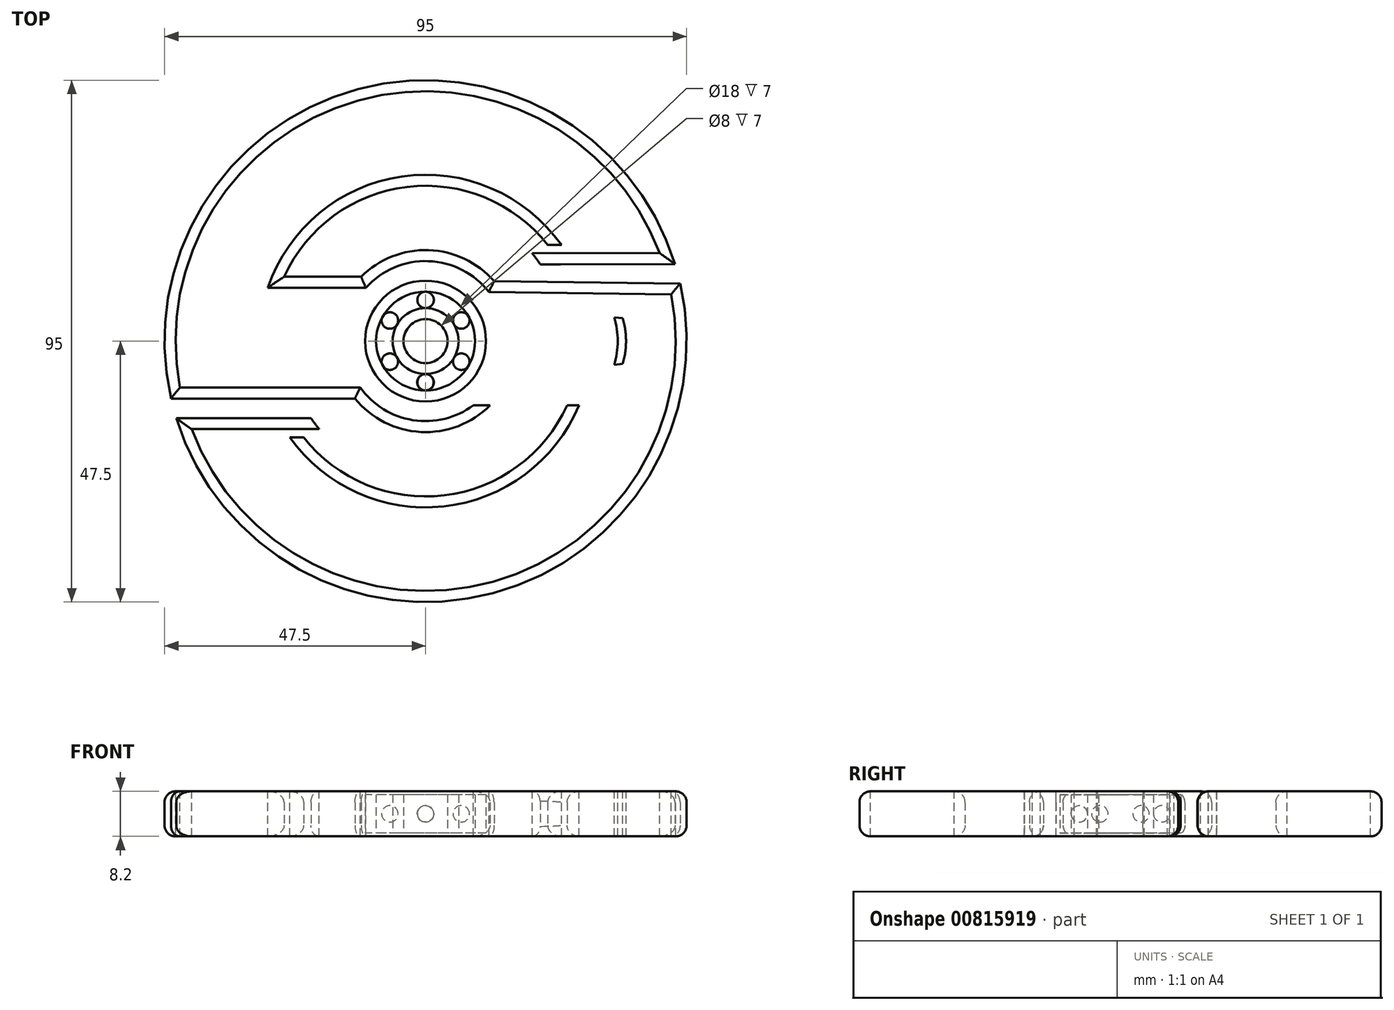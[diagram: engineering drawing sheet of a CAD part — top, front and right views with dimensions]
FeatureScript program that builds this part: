
annotation { "Feature Type Name" : "Feature", "Feature Type Description" : "" }
export const myFeature = defineFeature(function(context is Context, id is Id, definition is map)
    precondition{}
    {
        {
            var Q0;
            Q0=qCreatedBy(makeId("Top.planeOp"),FACE);
            var sketch = newSketch(context, id + "F0", { "sketchPlane" : qUnion([Q0])});
            skArc(sketch, "E0", {"start": v(45.38, 14.04) * mm, "mid": v(-10.46, 46.33) * mm, "end": v(-47, -6.81) * mm});
            skLineSegment(sketch, "E1.top", {"start": v(-45.38, -14.04) * mm, "end": v(-24.56, -14.04) * mm});
            skCircle(sketch, "E2", {"center": v(0, 0) * mm, "radius": 11.07 * mm});
            skArc(sketch, "E3", {"start": v(22.24, 17.5) * mm, "mid": v(-3.38, 28.09) * mm, "end": v(-25.75, 11.72) * mm});
            skArc(sketch, "E4.trimOffspring", {"start": v(-22.2, -17.54) * mm, "mid": v(3.4, -28.08) * mm, "end": v(25.75, -11.72) * mm});
            skArc(sketch, "E5.trimOffspring", {"start": v(-45.38, -14.04) * mm, "mid": v(10.5, -46.32) * mm, "end": v(47, 6.9) * mm});
            skLineSegment(sketch, "E6.trimOffspring", {"start": v(24.59, 14) * mm, "end": v(45.38, 14.04) * mm});
            skPoint(sketch, "E7.trimOffspring.end.orphan", {"position": v(45.38, -14.04) * mm});
            skPoint(sketch, "E1.bottom.start.orphan", {"position": v(-45.38, 14.04) * mm});
            skPoint(sketch, "E8.orphan", {"position": v(47, -6.9) * mm});
            skPoint(sketch, "E9.orphan", {"position": v(-47, 6.81) * mm});
            skArc(sketch, "E10", {"start": v(-12.86, -10.46) * mm, "mid": v(-0.85, -16.55) * mm, "end": v(11.72, -11.72) * mm});
            skArc(sketch, "E11.trimOffspring", {"start": v(12.47, 10.92) * mm, "mid": v(0.55, 16.57) * mm, "end": v(-11.72, 11.72) * mm});
            skLineSegment(sketch, "E12.trimOffspring", {"start": v(-8.7, 6.85) * mm, "end": v(8.59, 7) * mm});
            skLineSegment(sketch, "E13.trimOffspring", {"start": v(-8.7, -6.85) * mm, "end": v(8.69, -6.87) * mm});
            skLineSegment(sketch, "E14", {"start": v(-7.83, 7.83) * mm, "end": v(-6.87, 6.87) * mm});
            skLineSegment(sketch, "E15", {"start": v(6.87, -6.87) * mm, "end": v(7.83, -7.83) * mm});
            skLineSegment(sketch, "E16", {"start": v(-11.72, 11.72) * mm, "end": v(-25.75, 11.72) * mm});
            skLineSegment(sketch, "E17", {"start": v(11.72, -11.72) * mm, "end": v(11.72, -11.72) * mm});
            skArc(sketch, "E18", {"start": v(20.88, 14) * mm, "mid": v(19.54, 15.8) * mm, "end": v(18.05, 17.5) * mm});
            skLineSegment(sketch, "E19", {"start": v(-24.56, -14.04) * mm, "end": v(-20.85, -14.04) * mm});
            skLineSegment(sketch, "E20", {"start": v(24.59, 14) * mm, "end": v(20.88, 14) * mm});
            skLineSegment(sketch, "E21", {"start": v(22.24, 17.5) * mm, "end": v(18.05, 17.5) * mm});
            skLineSegment(sketch, "E22", {"start": v(-22.2, -17.54) * mm, "end": v(-18, -17.54) * mm});
            skArc(sketch, "E23.trimOffspring", {"start": v(-20.85, -14.04) * mm, "mid": v(-19.5, -15.85) * mm, "end": v(-18, -17.54) * mm});
            skLineSegment(sketch, "E24", {"start": v(0, 0) * mm, "end": v(0, 16.57) * mm, "construction": true});
            skLineSegment(sketch, "E25", {"start": v(-6.87, 6.87) * mm, "end": v(-11.72, 11.72) * mm, "construction": true});
            skLineSegment(sketch, "E26", {"start": v(0, 0) * mm, "end": v(11.72, 11.72) * mm, "construction": true});
            skLineSegment(sketch, "E27", {"start": v(6.87, -6.87) * mm, "end": v(11.72, -11.72) * mm, "construction": true});
            skLineSegment(sketch, "E28", {"start": v(0, 0) * mm, "end": v(0, -16.57) * mm, "construction": true});
            skLineSegment(sketch, "E29", {"start": v(0, 0) * mm, "end": v(-11.72, -11.72) * mm, "construction": true});
            skLineSegment(sketch, "E30.trimOffspring", {"start": v(-20, 20) * mm, "end": v(-33.59, 33.59) * mm, "construction": true});
            skLineSegment(sketch, "E31.trimOffspring", {"start": v(0, 28.29) * mm, "end": v(0, 47.5) * mm, "construction": true});
            skLineSegment(sketch, "E32.trimOffspring", {"start": v(20, 20) * mm, "end": v(33.59, 33.59) * mm, "construction": true});
            skLineSegment(sketch, "E33.trimOffspring", {"start": v(20, -20) * mm, "end": v(33.59, -33.59) * mm, "construction": true});
            skLineSegment(sketch, "E34.trimOffspring", {"start": v(0, -28.29) * mm, "end": v(0, -47.5) * mm, "construction": true});
            skLineSegment(sketch, "E35.trimOffspring", {"start": v(-20, -20) * mm, "end": v(-33.59, -33.59) * mm, "construction": true});
            skPoint(sketch, "E36", {"position": v(0, 37.9) * mm});
            skPoint(sketch, "E37", {"position": v(-26.8, 26.8) * mm});
            skPoint(sketch, "E38", {"position": v(26.8, 26.8) * mm});
            skPoint(sketch, "E39", {"position": v(26.8, -26.8) * mm});
            skPoint(sketch, "E40", {"position": v(0, -37.9) * mm});
            skPoint(sketch, "E41", {"position": v(-26.8, -26.8) * mm});
            skArc(sketch, "E42", {"start": v(-45.38, -14.04) * mm, "mid": v(10.5, -46.32) * mm, "end": v(47, 6.9) * mm, "construction": true});
            skArc(sketch, "E43", {"start": v(-47, -6.81) * mm, "mid": v(-46.7, -8.64) * mm, "end": v(-46.33, -10.46) * mm});
            skPoint(sketch, "E44", {"position": v(-46.33, -10.46) * mm});
            skArc(sketch, "E45", {"start": v(45.38, 14.04) * mm, "mid": v(-10.46, 46.33) * mm, "end": v(-47, -6.81) * mm, "construction": true});
            skArc(sketch, "E46", {"start": v(47, 6.9) * mm, "mid": v(46.7, 8.71) * mm, "end": v(46.32, 10.5) * mm});
            skPoint(sketch, "E47", {"position": v(46.32, 10.5) * mm});
            skLineSegment(sketch, "E48", {"start": v(-46.33, -10.46) * mm, "end": v(-36.42, -10.46) * mm});
            skLineSegment(sketch, "E49", {"start": v(46.32, 10.5) * mm, "end": v(12.47, 10.92) * mm});
            skPoint(sketch, "E50", {"position": v(-114.88, 3.23) * mm});
            skLineSegment(sketch, "E51.0", {"start": v(-114.88, 9.7) * mm, "end": v(-109.28, 6.47) * mm});
            skLineSegment(sketch, "E51.1", {"start": v(-109.28, 6.47) * mm, "end": v(-109.28, 0) * mm});
            skLineSegment(sketch, "E51.2", {"start": v(-109.28, 0) * mm, "end": v(-114.88, -3.23) * mm});
            skLineSegment(sketch, "E51.3", {"start": v(-114.88, -3.23) * mm, "end": v(-120.48, 0) * mm});
            skLineSegment(sketch, "E51.4", {"start": v(-120.48, 0) * mm, "end": v(-120.48, 6.47) * mm});
            skLineSegment(sketch, "E51.5", {"start": v(-120.48, 6.47) * mm, "end": v(-114.88, 9.7) * mm});
            skPoint(sketch, "E52", {"position": v(-130.27, -23) * mm});
            skLineSegment(sketch, "E53.0", {"start": v(-130.27, -16.53) * mm, "end": v(-124.67, -19.77) * mm});
            skLineSegment(sketch, "E53.1", {"start": v(-124.67, -19.77) * mm, "end": v(-124.67, -26.23) * mm});
            skLineSegment(sketch, "E53.2", {"start": v(-124.67, -26.23) * mm, "end": v(-130.27, -29.47) * mm});
            skLineSegment(sketch, "E53.3", {"start": v(-130.27, -29.47) * mm, "end": v(-135.87, -26.23) * mm});
            skLineSegment(sketch, "E53.4", {"start": v(-135.87, -26.23) * mm, "end": v(-135.87, -19.77) * mm});
            skLineSegment(sketch, "E53.5", {"start": v(-135.87, -19.77) * mm, "end": v(-130.27, -16.53) * mm});
            skLineSegment(sketch, "E54", {"start": v(-11.07, 0) * mm, "end": v(-47.5, 0) * mm, "construction": true});
            skLineSegment(sketch, "E55", {"start": v(11.07, 0) * mm, "end": v(47.5, 0) * mm, "construction": true});
            skLineSegment(sketch, "E56.0", {"start": v(-137.37, -18.9) * mm, "end": v(-130.27, -14.8) * mm});
            skLineSegment(sketch, "E56.1", {"start": v(-123.17, -18.9) * mm, "end": v(-123.17, -27.1) * mm});
            skLineSegment(sketch, "E56.2", {"start": v(-123.17, -27.1) * mm, "end": v(-130.27, -31.2) * mm});
            skLineSegment(sketch, "E56.3", {"start": v(-130.27, -14.8) * mm, "end": v(-123.17, -18.9) * mm});
            skLineSegment(sketch, "E56.4", {"start": v(-130.27, -31.2) * mm, "end": v(-137.37, -27.1) * mm});
            skLineSegment(sketch, "E56.5", {"start": v(-137.37, -27.1) * mm, "end": v(-137.37, -18.9) * mm});
            skLineSegment(sketch, "E57.0", {"start": v(-138.87, -18.03) * mm, "end": v(-130.27, -13.07) * mm});
            skLineSegment(sketch, "E57.1", {"start": v(-121.67, -18.03) * mm, "end": v(-121.67, -27.97) * mm});
            skLineSegment(sketch, "E57.2", {"start": v(-121.67, -27.97) * mm, "end": v(-130.27, -32.93) * mm});
            skLineSegment(sketch, "E57.3", {"start": v(-130.27, -13.07) * mm, "end": v(-121.67, -18.03) * mm});
            skLineSegment(sketch, "E57.4", {"start": v(-130.27, -32.93) * mm, "end": v(-138.87, -27.97) * mm});
            skLineSegment(sketch, "E57.5", {"start": v(-138.87, -27.97) * mm, "end": v(-138.87, -18.03) * mm});
            skPoint(sketch, "E58", {"position": v(-99.9, -24.26) * mm});
            skLineSegment(sketch, "E59.0", {"start": v(-109.83, -24.26) * mm, "end": v(-104.87, -15.66) * mm});
            skLineSegment(sketch, "E59.1", {"start": v(-94.94, -15.66) * mm, "end": v(-89.97, -24.26) * mm});
            skLineSegment(sketch, "E59.2", {"start": v(-89.97, -24.26) * mm, "end": v(-94.94, -32.86) * mm});
            skLineSegment(sketch, "E59.3", {"start": v(-104.87, -15.66) * mm, "end": v(-94.94, -15.66) * mm});
            skLineSegment(sketch, "E59.4", {"start": v(-94.94, -32.86) * mm, "end": v(-104.87, -32.86) * mm});
            skLineSegment(sketch, "E59.5", {"start": v(-104.87, -32.86) * mm, "end": v(-109.83, -24.26) * mm});
            skLineSegment(sketch, "E60.0", {"start": v(-107.82, -22.14) * mm, "end": v(-102.03, -16.34) * mm});
            skLineSegment(sketch, "E60.1", {"start": v(-94.1, -18.47) * mm, "end": v(-91.98, -26.38) * mm});
            skLineSegment(sketch, "E60.2", {"start": v(-91.98, -26.38) * mm, "end": v(-97.78, -32.18) * mm});
            skLineSegment(sketch, "E60.3", {"start": v(-102.03, -16.34) * mm, "end": v(-94.1, -18.47) * mm});
            skLineSegment(sketch, "E60.4", {"start": v(-97.78, -32.18) * mm, "end": v(-105.7, -30.06) * mm});
            skLineSegment(sketch, "E60.5", {"start": v(-105.7, -30.06) * mm, "end": v(-107.82, -22.14) * mm});
            skLineSegment(sketch, "E61.0", {"start": v(-99.9, -17.8) * mm, "end": v(-94.3, -21.03) * mm});
            skLineSegment(sketch, "E61.1", {"start": v(-94.3, -21.03) * mm, "end": v(-94.3, -27.5) * mm});
            skLineSegment(sketch, "E61.2", {"start": v(-94.3, -27.5) * mm, "end": v(-99.9, -30.73) * mm});
            skLineSegment(sketch, "E61.3", {"start": v(-99.9, -30.73) * mm, "end": v(-105.5, -27.5) * mm});
            skLineSegment(sketch, "E61.4", {"start": v(-105.5, -27.5) * mm, "end": v(-105.5, -21.03) * mm});
            skLineSegment(sketch, "E61.5", {"start": v(-105.5, -21.03) * mm, "end": v(-99.9, -17.8) * mm});
            skLineSegment(sketch, "E62.0", {"start": v(-111.57, -24.26) * mm, "end": v(-105.73, -14.16) * mm});
            skLineSegment(sketch, "E62.1", {"start": v(-94.07, -14.16) * mm, "end": v(-88.24, -24.26) * mm});
            skLineSegment(sketch, "E62.2", {"start": v(-88.24, -24.26) * mm, "end": v(-94.07, -34.36) * mm});
            skLineSegment(sketch, "E62.3", {"start": v(-105.73, -14.16) * mm, "end": v(-94.07, -14.16) * mm});
            skLineSegment(sketch, "E62.4", {"start": v(-94.07, -34.36) * mm, "end": v(-105.73, -34.36) * mm});
            skLineSegment(sketch, "E62.5", {"start": v(-105.73, -34.36) * mm, "end": v(-111.57, -24.26) * mm});
            skArc(sketch, "E63", {"start": v(-12.86, -10.46) * mm, "mid": v(16.55, -0.85) * mm, "end": v(-11.72, 11.72) * mm, "construction": true});
            skArc(sketch, "E64", {"start": v(-11.72, 11.72) * mm, "mid": v(-16.55, 0.85) * mm, "end": v(-12.86, -10.46) * mm, "construction": true});
            skLineSegment(sketch, "E65", {"start": v(11.72, -11.72) * mm, "end": v(25.75, -11.72) * mm});
            skLineSegment(sketch, "E66", {"start": v(12.47, 10.92) * mm, "end": v(12.47, 10.92) * mm});
            skArc(sketch, "E67", {"start": v(-20.87, 31.63) * mm, "mid": v(-26.8, 26.8) * mm, "end": v(-31.63, 20.87) * mm, "construction": true});
            skArc(sketch, "E68", {"start": v(-7.6, 37.12) * mm, "mid": v(-14.5, 35.01) * mm, "end": v(-20.87, 31.63) * mm, "construction": true});
            skArc(sketch, "E69", {"start": v(7.6, 37.12) * mm, "mid": v(0, 37.9) * mm, "end": v(-7.6, 37.12) * mm, "construction": true});
            skArc(sketch, "E70", {"start": v(20.87, 31.63) * mm, "mid": v(14.5, 35.01) * mm, "end": v(7.6, 37.12) * mm, "construction": true});
            skCircle(sketch, "E71", {"center": v(-14.5, 35.01) * mm, "radius": 2.5 * mm});
            skCircle(sketch, "E72", {"center": v(14.5, 35.01) * mm, "radius": 2.5 * mm});
            skCircle(sketch, "E73.MirrorC", {"center": v(-14.5, -35.01) * mm, "radius": 2.5 * mm});
            skCircle(sketch, "E74.MirrorC", {"center": v(14.5, -35.01) * mm, "radius": 2.5 * mm});
            skLineSegment(sketch, "E75", {"start": v(-31.63, 20.87) * mm, "end": v(-31.63, 20.87) * mm});
            skLineSegment(sketch, "E76", {"start": v(-36.42, -10.46) * mm, "end": v(-12.86, -10.46) * mm});
            skPoint(sketch, "E77", {"position": v(-31.63, 20.87) * mm});
            skPoint(sketch, "E78", {"position": v(-36.42, -10.46) * mm});
            skArc(sketch, "E79", {"start": v(-31.63, 20.87) * mm, "mid": v(-37.46, 5.73) * mm, "end": v(-36.42, -10.46) * mm, "construction": true});
            skArc(sketch, "E80", {"start": v(-36.42, -10.46) * mm, "mid": v(22.43, -30.54) * mm, "end": v(20.87, 31.63) * mm, "construction": true});
            skPoint(sketch, "E81", {"position": v(-33.09, 18.48) * mm});
            skLineSegment(sketch, "E82.0", {"start": v(-66.3, -4.13) * mm, "end": v(-66.3, 4.13) * mm});
            skLineSegment(sketch, "E82.1", {"start": v(-66.3, 4.13) * mm, "end": v(-59.15, 8.26) * mm});
            skLineSegment(sketch, "E82.2", {"start": v(-59.15, 8.26) * mm, "end": v(-52, 4.13) * mm});
            skLineSegment(sketch, "E82.3", {"start": v(-52, 4.13) * mm, "end": v(-52, -4.13) * mm});
            skLineSegment(sketch, "E82.4", {"start": v(-52, -4.13) * mm, "end": v(-59.15, -8.26) * mm});
            skLineSegment(sketch, "E82.5", {"start": v(-59.15, -8.26) * mm, "end": v(-66.3, -4.13) * mm});
            skPoint(sketch, "E82.0.midPoint", {"position": v(-66.3, 0) * mm});
            skPoint(sketch, "E83", {"position": v(-59.15, 0) * mm});
            skLineSegment(sketch, "E84.0", {"start": v(-25.96, -63.18) * mm, "end": v(-30.08, -56.03) * mm});
            skLineSegment(sketch, "E84.1", {"start": v(-30.08, -56.03) * mm, "end": v(-25.96, -48.88) * mm});
            skLineSegment(sketch, "E84.2", {"start": v(-25.96, -48.88) * mm, "end": v(-17.7, -48.88) * mm});
            skLineSegment(sketch, "E84.3", {"start": v(-17.7, -48.88) * mm, "end": v(-13.57, -56.03) * mm});
            skLineSegment(sketch, "E84.4", {"start": v(-13.57, -56.03) * mm, "end": v(-17.7, -63.18) * mm});
            skLineSegment(sketch, "E84.5", {"start": v(-17.7, -63.18) * mm, "end": v(-25.96, -63.18) * mm});
            skPoint(sketch, "E84.0.midPoint", {"position": v(-28.02, -59.6) * mm});
            skPoint(sketch, "E85", {"position": v(-21.83, -56.03) * mm});
            skLineSegment(sketch, "E86.0", {"start": v(-4.13, -45.04) * mm, "end": v(-8.26, -37.9) * mm});
            skLineSegment(sketch, "E86.1", {"start": v(-8.26, -37.9) * mm, "end": v(-4.13, -30.74) * mm});
            skLineSegment(sketch, "E86.2", {"start": v(-4.13, -30.74) * mm, "end": v(4.13, -30.74) * mm});
            skLineSegment(sketch, "E86.3", {"start": v(4.13, -30.74) * mm, "end": v(8.26, -37.9) * mm});
            skLineSegment(sketch, "E86.4", {"start": v(8.26, -37.9) * mm, "end": v(4.13, -45.04) * mm});
            skLineSegment(sketch, "E86.5", {"start": v(4.13, -45.04) * mm, "end": v(-4.13, -45.04) * mm});
            skPoint(sketch, "E86.0.midPoint", {"position": v(-6.2, -41.47) * mm});
            skLineSegment(sketch, "E87.0", {"start": v(-4.13, 30.74) * mm, "end": v(-8.26, 37.9) * mm});
            skLineSegment(sketch, "E87.1", {"start": v(-8.26, 37.9) * mm, "end": v(-4.13, 45.04) * mm});
            skLineSegment(sketch, "E87.2", {"start": v(-4.13, 45.04) * mm, "end": v(4.13, 45.04) * mm});
            skLineSegment(sketch, "E87.3", {"start": v(4.13, 45.04) * mm, "end": v(8.26, 37.9) * mm});
            skLineSegment(sketch, "E87.4", {"start": v(8.26, 37.9) * mm, "end": v(4.13, 30.74) * mm});
            skLineSegment(sketch, "E87.5", {"start": v(4.13, 30.74) * mm, "end": v(-4.13, 30.74) * mm});
            skPoint(sketch, "E87.0.midPoint", {"position": v(-6.2, 34.32) * mm});
            skLineSegment(sketch, "E88.0", {"start": v(-76.52, -68.25) * mm, "end": v(-84.5, -66.1) * mm});
            skLineSegment(sketch, "E88.1", {"start": v(-84.5, -66.1) * mm, "end": v(-86.63, -58.13) * mm});
            skLineSegment(sketch, "E88.2", {"start": v(-86.63, -58.13) * mm, "end": v(-80.8, -52.3) * mm});
            skLineSegment(sketch, "E88.3", {"start": v(-80.8, -52.3) * mm, "end": v(-72.82, -54.43) * mm});
            skLineSegment(sketch, "E88.4", {"start": v(-72.82, -54.43) * mm, "end": v(-70.68, -62.4) * mm});
            skLineSegment(sketch, "E88.5", {"start": v(-70.68, -62.4) * mm, "end": v(-76.52, -68.25) * mm});
            skPoint(sketch, "E88.0.midPoint", {"position": v(-80.5, -67.18) * mm});
            skPoint(sketch, "E89", {"position": v(-78.66, -60.27) * mm});
            skLineSegment(sketch, "E90.0", {"start": v(-24.66, 18.82) * mm, "end": v(-32.63, 20.96) * mm});
            skLineSegment(sketch, "E90.1", {"start": v(-32.63, 20.96) * mm, "end": v(-34.77, 28.93) * mm});
            skLineSegment(sketch, "E90.2", {"start": v(-34.77, 28.93) * mm, "end": v(-28.93, 34.77) * mm});
            skLineSegment(sketch, "E90.3", {"start": v(-28.93, 34.77) * mm, "end": v(-20.96, 32.63) * mm});
            skLineSegment(sketch, "E90.4", {"start": v(-20.96, 32.63) * mm, "end": v(-18.82, 24.66) * mm});
            skLineSegment(sketch, "E90.5", {"start": v(-18.82, 24.66) * mm, "end": v(-24.66, 18.82) * mm});
            skPoint(sketch, "E90.0.midPoint", {"position": v(-28.65, 19.89) * mm});
            skLineSegment(sketch, "E91.0", {"start": v(28.93, -34.77) * mm, "end": v(20.96, -32.63) * mm});
            skLineSegment(sketch, "E91.1", {"start": v(20.96, -32.63) * mm, "end": v(18.82, -24.66) * mm});
            skLineSegment(sketch, "E91.2", {"start": v(18.82, -24.66) * mm, "end": v(24.66, -18.82) * mm});
            skLineSegment(sketch, "E91.3", {"start": v(24.66, -18.82) * mm, "end": v(32.63, -20.96) * mm});
            skLineSegment(sketch, "E91.4", {"start": v(32.63, -20.96) * mm, "end": v(34.77, -28.93) * mm});
            skLineSegment(sketch, "E91.5", {"start": v(34.77, -28.93) * mm, "end": v(28.93, -34.77) * mm});
            skPoint(sketch, "E91.0.midPoint", {"position": v(24.95, -33.7) * mm});
            skLineSegment(sketch, "E92.0", {"start": v(-34.77, -28.93) * mm, "end": v(-32.63, -20.96) * mm});
            skLineSegment(sketch, "E92.1", {"start": v(-32.63, -20.96) * mm, "end": v(-24.66, -18.82) * mm});
            skLineSegment(sketch, "E92.2", {"start": v(-24.66, -18.82) * mm, "end": v(-18.82, -24.66) * mm});
            skLineSegment(sketch, "E92.3", {"start": v(-18.82, -24.66) * mm, "end": v(-20.96, -32.63) * mm});
            skLineSegment(sketch, "E92.4", {"start": v(-20.96, -32.63) * mm, "end": v(-28.93, -34.77) * mm});
            skLineSegment(sketch, "E92.5", {"start": v(-28.93, -34.77) * mm, "end": v(-34.77, -28.93) * mm});
            skPoint(sketch, "E92.0.midPoint", {"position": v(-33.7, -24.95) * mm});
            skLineSegment(sketch, "E93.0", {"start": v(18.82, 24.66) * mm, "end": v(20.96, 32.63) * mm});
            skLineSegment(sketch, "E93.1", {"start": v(20.96, 32.63) * mm, "end": v(28.93, 34.77) * mm});
            skLineSegment(sketch, "E93.2", {"start": v(28.93, 34.77) * mm, "end": v(34.77, 28.93) * mm});
            skLineSegment(sketch, "E93.3", {"start": v(34.77, 28.93) * mm, "end": v(32.63, 20.96) * mm});
            skLineSegment(sketch, "E93.4", {"start": v(32.63, 20.96) * mm, "end": v(24.66, 18.82) * mm});
            skLineSegment(sketch, "E93.5", {"start": v(24.66, 18.82) * mm, "end": v(18.82, 24.66) * mm});
            skPoint(sketch, "E93.0.midPoint", {"position": v(19.89, 28.65) * mm});
            skSolve(sketch);
        }
        {
            var Q0;
            Q0=makeQuery(id+"F0.imprint","IMPRINT",FACE,{"disambiguationData":[TD([[makeQuery(id+"F0.imprint","IMPRINT",EDGE,{"derivedFrom":sQuery(id+"F0.wireOp",EDGE,"E0")}),1.0]])]});
            extrude(context, id + "F1", {"entities" : qUnion([Q0]), "endBound" : BoundingType.SYMMETRIC, "depth" : 8.2 * mm, "offsetDistance" : 25 * mm});
        }
        {
            var Q0;
            Q0=makeQuery(id+"F1.opExtrude","CAP_EDGE",EDGE,{"disambiguationData":[OSD([sQuery(id+"F0.wireOp",EDGE,"E0")])],"isStart":false});
            var Q1;
            Q1=makeQuery(id+"F1.opExtrude","CAP_EDGE",EDGE,{"disambiguationData":[OSD([sQuery(id+"F0.wireOp",EDGE,"E5.trimOffspring")])],"isStart":false});
            var Q2;
            Q2=makeQuery(id+"F1.opExtrude","CAP_EDGE",EDGE,{"disambiguationData":[OSD([sQuery(id+"F0.wireOp",EDGE,"E0")])],"isStart":true});
            var Q3;
            Q3=makeQuery(id+"F1.opExtrude","CAP_EDGE",EDGE,{"disambiguationData":[OSD([sQuery(id+"F0.wireOp",EDGE,"E5.trimOffspring")])],"isStart":true});
            var Q4;
            Q4=makeQuery(id+"F1.opExtrude","CAP_EDGE",EDGE,{"disambiguationData":[OSD([sQuery(id+"F0.wireOp",EDGE,"E1.top"),sQuery(id+"F0.wireOp",EDGE,"E19")])],"isStart":true});
            var Q5;
            Q5=makeQuery(id+"F1.opExtrude","CAP_EDGE",EDGE,{"disambiguationData":[OSD([sQuery(id+"F0.wireOp",EDGE,"E1.top"),sQuery(id+"F0.wireOp",EDGE,"E19")])],"isStart":false});
            var Q6;
            Q6=makeQuery(id+"F1.opExtrude","CAP_EDGE",EDGE,{"disambiguationData":[OSD([sQuery(id+"F0.wireOp",EDGE,"af73f036-c247-4c71-b03d-1512b0a657ec.trimOffspring")])],"isStart":true});
            var Q7;
            Q7=makeQuery(id+"F1.opExtrude","CAP_EDGE",EDGE,{"disambiguationData":[OSD([sQuery(id+"F0.wireOp",EDGE,"af73f036-c247-4c71-b03d-1512b0a657ec.trimOffspring")])],"isStart":false});
            var Q8;
            Q8=makeQuery(id+"F1.opExtrude","CAP_EDGE",EDGE,{"disambiguationData":[OSD([sQuery(id+"F0.wireOp",EDGE,"E11.trimOffspring")])],"isStart":false});
            var Q9;
            Q9=makeQuery(id+"F1.opExtrude","CAP_EDGE",EDGE,{"disambiguationData":[OSD([sQuery(id+"F0.wireOp",EDGE,"E11.trimOffspring")])],"isStart":true});
            var Q10;
            Q10=makeQuery(id+"F1.opExtrude","CAP_EDGE",EDGE,{"disambiguationData":[OSD([sQuery(id+"F0.wireOp",EDGE,"E16")])],"isStart":false});
            var Q11;
            Q11=makeQuery(id+"F1.opExtrude","CAP_EDGE",EDGE,{"disambiguationData":[OSD([sQuery(id+"F0.wireOp",EDGE,"E16")])],"isStart":true});
            var Q12;
            Q12=makeQuery(id+"F1.opExtrude","CAP_EDGE",EDGE,{"disambiguationData":[OSD([sQuery(id+"F0.wireOp",EDGE,"E4.trimOffspring")])],"isStart":true});
            var Q13;
            Q13=makeQuery(id+"F1.opExtrude","CAP_EDGE",EDGE,{"disambiguationData":[OSD([sQuery(id+"F0.wireOp",EDGE,"E4.trimOffspring")])],"isStart":false});
            var Q14;
            Q14=makeQuery(id+"F1.opExtrude","CAP_EDGE",EDGE,{"disambiguationData":[OSD([sQuery(id+"F0.wireOp",EDGE,"E3")])],"isStart":false});
            var Q15;
            Q15=makeQuery(id+"F1.opExtrude","CAP_EDGE",EDGE,{"disambiguationData":[OSD([sQuery(id+"F0.wireOp",EDGE,"E3")])],"isStart":true});
            var Q16;
            Q16=makeQuery(id+"F1.opExtrude","CAP_EDGE",EDGE,{"disambiguationData":[OSD([sQuery(id+"F0.wireOp",EDGE,"E17")])],"isStart":false});
            var Q17;
            Q17=makeQuery(id+"F1.opExtrude","CAP_EDGE",EDGE,{"disambiguationData":[OSD([sQuery(id+"F0.wireOp",EDGE,"E17")])],"isStart":true});
            var Q18;
            Q18=makeQuery(id+"F1.opExtrude","CAP_EDGE",EDGE,{"disambiguationData":[OSD([sQuery(id+"F0.wireOp",EDGE,"E10")])],"isStart":false});
            var Q19;
            Q19=makeQuery(id+"F1.opExtrude","CAP_EDGE",EDGE,{"disambiguationData":[OSD([sQuery(id+"F0.wireOp",EDGE,"E10")])],"isStart":true});
            var Q20;
            Q20=makeQuery(id+"F1.opExtrude","CAP_EDGE",EDGE,{"disambiguationData":[OSD([sQuery(id+"F0.wireOp",EDGE,"318f1a37-417c-41ab-8845-f020125537680.MirrorCS")])],"isStart":false});
            var Q21;
            Q21=makeQuery(id+"F1.opExtrude","CAP_EDGE",EDGE,{"disambiguationData":[OSD([sQuery(id+"F0.wireOp",EDGE,"318f1a37-417c-41ab-8845-f020125537680.MirrorCS")])],"isStart":true});
            var Q22;
            Q22=makeQuery(id+"F1.opExtrude","CAP_EDGE",EDGE,{"disambiguationData":[OSD([sQuery(id+"F0.wireOp",EDGE,"E6.trimOffspring")])],"isStart":false});
            var Q23;
            Q23=makeQuery(id+"F1.opExtrude","CAP_EDGE",EDGE,{"disambiguationData":[OSD([sQuery(id+"F0.wireOp",EDGE,"E6.trimOffspring")])],"isStart":true});
            var Q24;
            Q24=makeQuery(id+"F1.opExtrude","CAP_EDGE",EDGE,{"disambiguationData":[OSD([sQuery(id+"F0.wireOp",EDGE,"E48")])],"isStart":false});
            var Q25;
            Q25=makeQuery(id+"F1.opExtrude","CAP_EDGE",EDGE,{"disambiguationData":[OSD([sQuery(id+"F0.wireOp",EDGE,"E48")])],"isStart":true});
            var Q26;
            Q26=makeQuery(id+"F1.opExtrude","CAP_EDGE",EDGE,{"disambiguationData":[OSD([sQuery(id+"F0.wireOp",EDGE,"E49")])],"isStart":true});
            var Q27;
            Q27=makeQuery(id+"F1.opExtrude","CAP_EDGE",EDGE,{"disambiguationData":[OSD([sQuery(id+"F0.wireOp",EDGE,"E49")])],"isStart":false});
            fillet(context, id + "F2", {"entities" : qUnion([Q0, Q1, Q2, Q3, Q4, Q5, Q6, Q7, Q8, Q9, Q10, Q11, Q12, Q13, Q14, Q15, Q16, Q17, Q18, Q19, Q20, Q21, Q22, Q23, Q24, Q25, Q26, Q27]), "radius" : 2 * mm, "tangentPropagation" : true, "allowEdgeOverflow" : false});
        }
        {
            var Q0;
            Q0=qCreatedBy(makeId("Top.planeOp"),FACE);
            var sketch = newSketch(context, id + "F3", { "sketchPlane" : qUnion([Q0])});
            skCircle(sketch, "E94", {"center": v(56.9, -63.65) * mm, "radius": 11 * mm});
            skCircle(sketch, "E95", {"center": v(56.9, -63.65) * mm, "radius": 9 * mm});
            skCircle(sketch, "E96", {"center": v(56.9, -63.65) * mm, "radius": 4 * mm});
            skCircle(sketch, "E97", {"center": v(56.9, -63.65) * mm, "radius": 6 * mm});
            skArc(sketch, "E98", {"start": v(56.9, -57.65) * mm, "mid": v(58.4, -56.15) * mm, "end": v(56.9, -54.65) * mm});
            skArc(sketch, "E99.1.0", {"start": v(63.4, -61.4) * mm, "mid": v(64.9, -59.9) * mm, "end": v(63.4, -58.4) * mm});
            skArc(sketch, "E99.2.0", {"start": v(63.4, -68.9) * mm, "mid": v(64.9, -67.4) * mm, "end": v(63.4, -65.9) * mm});
            skArc(sketch, "E99.3.0", {"start": v(56.9, -72.65) * mm, "mid": v(58.4, -71.14) * mm, "end": v(56.88, -69.65) * mm});
            skArc(sketch, "E99.4.0", {"start": v(50.41, -68.9) * mm, "mid": v(51.91, -67.4) * mm, "end": v(50.41, -65.9) * mm});
            skArc(sketch, "E99.5.0", {"start": v(50.41, -61.4) * mm, "mid": v(51.91, -59.9) * mm, "end": v(50.41, -58.4) * mm});
            skLineSegment(sketch, "E100", {"start": v(50.41, -65.9) * mm, "end": v(50.41, -68.9) * mm});
            skLineSegment(sketch, "E101", {"start": v(56.88, -69.65) * mm, "end": v(56.9, -72.65) * mm});
            skLineSegment(sketch, "E102", {"start": v(63.4, -65.9) * mm, "end": v(63.4, -68.9) * mm});
            skLineSegment(sketch, "E103", {"start": v(63.4, -58.4) * mm, "end": v(63.4, -61.4) * mm});
            skLineSegment(sketch, "E104", {"start": v(56.9, -54.65) * mm, "end": v(56.9, -54.65) * mm});
            skLineSegment(sketch, "E105", {"start": v(50.41, -58.4) * mm, "end": v(50.41, -61.4) * mm});
            skLineSegment(sketch, "E106.trimOffspring", {"start": v(56.9, -57.65) * mm, "end": v(56.9, -57.65) * mm});
            skLineSegment(sketch, "E107.trimOffspring", {"start": v(51.71, -60.65) * mm, "end": v(51.71, -60.65) * mm});
            skLineSegment(sketch, "E108", {"start": v(56.9, -57.65) * mm, "end": v(56.9, -54.65) * mm});
            skSolve(sketch);
        }
        {
            var Q0;
            Q0=makeQuery(id+"F3.imprint","IMPRINT",FACE,{"disambiguationData":[TD([[makeQuery(id+"F3.imprint","IMPRINT",EDGE,{"derivedFrom":sQuery(id+"F3.wireOp",EDGE,"E94")}),1.0]])]});
            var Q1;
            Q1=makeQuery(id+"F3.imprint","IMPRINT",FACE,{"disambiguationData":[TD([[makeQuery(id+"F3.imprint","IMPRINT",EDGE,{"derivedFrom":sQuery(id+"F3.wireOp",EDGE,"E96")}),-1.0]])]});
            extrude(context, id + "F4", {"entities" : qUnion([Q0, Q1]), "endBound" : BoundingType.SYMMETRIC, "depth" : 7 * mm, "offsetDistance" : 25 * mm});
        }
        {
            var Q0;
            Q0=makeQuery(id+"F3.imprint","IMPRINT",FACE,{"disambiguationData":[TD([[makeQuery(id+"F3.imprint","IMPRINT",EDGE,{"derivedFrom":sQuery(id+"F3.wireOp",EDGE,"E98")}),1.0]])]});
            var Q1;
            Q1=sQuery(id+"F3.wireOp",EDGE,"E108");
            revolve(context, id + "F5", {"surfaceOperationType" : NewSurfaceOperationType.NEW, "entities" : qUnion([Q0]), "axis" : qUnion([Q1]), "revolveType" : RevolveType.FULL});
        }
        {
            var Q0;
            {var subQ0=sQuery(id+"F3.wireOp",EDGE,"E103");Q0=makeQuery(id+"F3.imprint","IMPRINT",FACE,{"disambiguationData":[TD([[makeQuery(id+"F3.imprint","IMPRINT",EDGE,{"derivedFrom":subQ0}),1.0]])]});}
            var Q1;
            Q1=sQuery(id+"F3.wireOp",EDGE,"E103");
            revolve(context, id + "F6", {"surfaceOperationType" : NewSurfaceOperationType.NEW, "entities" : qUnion([Q0]), "axis" : qUnion([Q1]), "revolveType" : RevolveType.FULL});
        }
        {
            var Q0;
            {var subQ0=sQuery(id+"F3.wireOp",EDGE,"E105");Q0=makeQuery(id+"F3.imprint","IMPRINT",FACE,{"disambiguationData":[TD([[makeQuery(id+"F3.imprint","IMPRINT",EDGE,{"derivedFrom":subQ0}),1.0]])]});}
            var Q1;
            Q1=sQuery(id+"F3.wireOp",EDGE,"E105");
            revolve(context, id + "F7", {"surfaceOperationType" : NewSurfaceOperationType.NEW, "entities" : qUnion([Q0]), "axis" : qUnion([Q1]), "revolveType" : RevolveType.FULL});
        }
        {
            var Q0;
            {var subQ0=sQuery(id+"F3.wireOp",EDGE,"E100");Q0=makeQuery(id+"F3.imprint","IMPRINT",FACE,{"disambiguationData":[TD([[makeQuery(id+"F3.imprint","IMPRINT",EDGE,{"derivedFrom":subQ0}),1.0]])]});}
            var Q1;
            Q1=sQuery(id+"F3.wireOp",EDGE,"E100");
            revolve(context, id + "F8", {"surfaceOperationType" : NewSurfaceOperationType.NEW, "entities" : qUnion([Q0]), "axis" : qUnion([Q1]), "revolveType" : RevolveType.FULL});
        }
        {
            var Q0;
            {var subQ0=sQuery(id+"F3.wireOp",EDGE,"E102");Q0=makeQuery(id+"F3.imprint","IMPRINT",FACE,{"disambiguationData":[TD([[makeQuery(id+"F3.imprint","IMPRINT",EDGE,{"derivedFrom":subQ0}),1.0]])]});}
            var Q1;
            Q1=sQuery(id+"F3.wireOp",EDGE,"E102");
            revolve(context, id + "F9", {"surfaceOperationType" : NewSurfaceOperationType.NEW, "entities" : qUnion([Q0]), "axis" : qUnion([Q1]), "revolveType" : RevolveType.FULL});
        }
        {
            var Q0;
            {var subQ0=sQuery(id+"F3.wireOp",EDGE,"E101");Q0=makeQuery(id+"F3.imprint","IMPRINT",FACE,{"disambiguationData":[TD([[makeQuery(id+"F3.imprint","IMPRINT",EDGE,{"derivedFrom":subQ0}),1.0]])]});}
            var Q1;
            Q1=sQuery(id+"F3.wireOp",EDGE,"E101");
            revolve(context, id + "F10", {"surfaceOperationType" : NewSurfaceOperationType.NEW, "entities" : qUnion([Q0]), "axis" : qUnion([Q1]), "revolveType" : RevolveType.FULL});
        }
        {
            var Q0;
            Q0=makeQuery(id+"F6.opRevolve","SWEPT_BODY",BODY,{"disambiguationData":[OSD([sQuery(id+"F3.wireOp",EDGE,"E99.1.0"),sQuery(id+"F3.wireOp",EDGE,"E103")])]});
            var Q1;
            Q1=makeQuery(id+"F5.opRevolve","SWEPT_BODY",BODY,{"disambiguationData":[OSD([sQuery(id+"F3.wireOp",EDGE,"E98"),sQuery(id+"F3.wireOp",EDGE,"E108")])]});
            var Q2;
            Q2=makeQuery(id+"F4.opExtrude","SWEPT_BODY",BODY,{"disambiguationData":[OSD([sQuery(id+"F3.wireOp",EDGE,"E96"),sQuery(id+"F3.wireOp",EDGE,"E97")])]});
            var Q3;
            Q3=makeQuery(id+"F9.opRevolve","SWEPT_BODY",BODY,{"disambiguationData":[OSD([sQuery(id+"F3.wireOp",EDGE,"E99.2.0"),sQuery(id+"F3.wireOp",EDGE,"E102")])]});
            var Q4;
            Q4=makeQuery(id+"F7.opRevolve","SWEPT_BODY",BODY,{"disambiguationData":[OSD([sQuery(id+"F3.wireOp",EDGE,"E99.5.0"),sQuery(id+"F3.wireOp",EDGE,"E105")])]});
            var Q5;
            Q5=makeQuery(id+"F4.opExtrude","SWEPT_BODY",BODY,{"disambiguationData":[OSD([sQuery(id+"F3.wireOp",EDGE,"E94"),sQuery(id+"F3.wireOp",EDGE,"E95")])]});
            var Q6;
            Q6=makeQuery(id+"F10.opRevolve","SWEPT_BODY",BODY,{"disambiguationData":[OSD([sQuery(id+"F3.wireOp",EDGE,"E99.3.0"),sQuery(id+"F3.wireOp",EDGE,"E101")])]});
            var Q7;
            Q7=makeQuery(id+"F8.opRevolve","SWEPT_BODY",BODY,{"disambiguationData":[OSD([sQuery(id+"F3.wireOp",EDGE,"E99.4.0"),sQuery(id+"F3.wireOp",EDGE,"E100")])]});
            transform(context, id + "F11", {"entities" : qUnion([Q0, Q1, Q2, Q3, Q4, Q5, Q6, Q7]), "transformType" : TransformType.TRANSLATION_3D, "dx" : -56.9 * mm, "dy" : 63.65 * mm, "dz" : 0 * mm, "makeCopy" : false});
        }
        {
            var Q0;
            Q0=makeQuery(id+"F1.opExtrude","SWEPT_EDGE",EDGE,{"disambiguationData":[OSD([sQuery(id+"F0.wireOp",EDGE,"E18"),sQuery(id+"F0.wireOp",EDGE,"E21")])]});
            var Q1;
            Q1=makeQuery(id+"F1.opExtrude","SWEPT_EDGE",EDGE,{"disambiguationData":[OSD([sQuery(id+"F0.wireOp",EDGE,"E22"),sQuery(id+"F0.wireOp",EDGE,"E23.trimOffspring")])]});
            fillet(context, id + "F12", {"entities" : qUnion([Q0, Q1]), "radius" : 1 * mm, "tangentPropagation" : true, "allowEdgeOverflow" : false});
        }
        {
            var Q0;
            Q0=makeQuery(id+"F1.opExtrude","CAP_FACE",FACE,{"disambiguationData":[OSD([sQuery(id+"F0.wireOp",EDGE,"E0"),sQuery(id+"F0.wireOp",EDGE,"E1.top"),sQuery(id+"F0.wireOp",EDGE,"E2"),sQuery(id+"F0.wireOp",EDGE,"E3"),sQuery(id+"F0.wireOp",EDGE,"E4.trimOffspring"),sQuery(id+"F0.wireOp",EDGE,"E5.trimOffspring"),sQuery(id+"F0.wireOp",EDGE,"E6.trimOffspring"),sQuery(id+"F0.wireOp",EDGE,"E10"),sQuery(id+"F0.wireOp",EDGE,"E11.trimOffspring"),sQuery(id+"F0.wireOp",EDGE,"E16"),sQuery(id+"F0.wireOp",EDGE,"E18"),sQuery(id+"F0.wireOp",EDGE,"E19"),sQuery(id+"F0.wireOp",EDGE,"E20"),sQuery(id+"F0.wireOp",EDGE,"E21"),sQuery(id+"F0.wireOp",EDGE,"E22"),sQuery(id+"F0.wireOp",EDGE,"E23.trimOffspring"),sQuery(id+"F0.wireOp",EDGE,"392220d0-4b47-404b-b555-e27dfb5f0e7a.0"),sQuery(id+"F0.wireOp",EDGE,"392220d0-4b47-404b-b555-e27dfb5f0e7a.1"),sQuery(id+"F0.wireOp",EDGE,"392220d0-4b47-404b-b555-e27dfb5f0e7a.2"),sQuery(id+"F0.wireOp",EDGE,"392220d0-4b47-404b-b555-e27dfb5f0e7a.3"),sQuery(id+"F0.wireOp",EDGE,"392220d0-4b47-404b-b555-e27dfb5f0e7a.4"),sQuery(id+"F0.wireOp",EDGE,"392220d0-4b47-404b-b555-e27dfb5f0e7a.5"),sQuery(id+"F0.wireOp",EDGE,"2f86eadb-132a-42d0-bef6-e62a83f4e276.0"),sQuery(id+"F0.wireOp",EDGE,"2f86eadb-132a-42d0-bef6-e62a83f4e276.1"),sQuery(id+"F0.wireOp",EDGE,"2f86eadb-132a-42d0-bef6-e62a83f4e276.2"),sQuery(id+"F0.wireOp",EDGE,"2f86eadb-132a-42d0-bef6-e62a83f4e276.3"),sQuery(id+"F0.wireOp",EDGE,"2f86eadb-132a-42d0-bef6-e62a83f4e276.4"),sQuery(id+"F0.wireOp",EDGE,"2f86eadb-132a-42d0-bef6-e62a83f4e276.5"),sQuery(id+"F0.wireOp",EDGE,"86e7703e-a9ac-4136-99b0-15613d8deff7.0"),sQuery(id+"F0.wireOp",EDGE,"86e7703e-a9ac-4136-99b0-15613d8deff7.1"),sQuery(id+"F0.wireOp",EDGE,"86e7703e-a9ac-4136-99b0-15613d8deff7.2"),sQuery(id+"F0.wireOp",EDGE,"86e7703e-a9ac-4136-99b0-15613d8deff7.3"),sQuery(id+"F0.wireOp",EDGE,"86e7703e-a9ac-4136-99b0-15613d8deff7.4"),sQuery(id+"F0.wireOp",EDGE,"86e7703e-a9ac-4136-99b0-15613d8deff7.5"),sQuery(id+"F0.wireOp",EDGE,"b7a0bb4e-0e0c-4cd5-984e-c85507769997.0"),sQuery(id+"F0.wireOp",EDGE,"b7a0bb4e-0e0c-4cd5-984e-c85507769997.1"),sQuery(id+"F0.wireOp",EDGE,"b7a0bb4e-0e0c-4cd5-984e-c85507769997.2"),sQuery(id+"F0.wireOp",EDGE,"b7a0bb4e-0e0c-4cd5-984e-c85507769997.3"),sQuery(id+"F0.wireOp",EDGE,"b7a0bb4e-0e0c-4cd5-984e-c85507769997.4"),sQuery(id+"F0.wireOp",EDGE,"b7a0bb4e-0e0c-4cd5-984e-c85507769997.5"),sQuery(id+"F0.wireOp",EDGE,"9a74dc4f-569b-4c7d-9947-54b7030d0dd2.0"),sQuery(id+"F0.wireOp",EDGE,"9a74dc4f-569b-4c7d-9947-54b7030d0dd2.1"),sQuery(id+"F0.wireOp",EDGE,"9a74dc4f-569b-4c7d-9947-54b7030d0dd2.2"),sQuery(id+"F0.wireOp",EDGE,"9a74dc4f-569b-4c7d-9947-54b7030d0dd2.3"),sQuery(id+"F0.wireOp",EDGE,"9a74dc4f-569b-4c7d-9947-54b7030d0dd2.4"),sQuery(id+"F0.wireOp",EDGE,"9a74dc4f-569b-4c7d-9947-54b7030d0dd2.5"),sQuery(id+"F0.wireOp",EDGE,"f3070712-bb4c-4e14-84f0-c401675ae4b3.0"),sQuery(id+"F0.wireOp",EDGE,"f3070712-bb4c-4e14-84f0-c401675ae4b3.1"),sQuery(id+"F0.wireOp",EDGE,"f3070712-bb4c-4e14-84f0-c401675ae4b3.2"),sQuery(id+"F0.wireOp",EDGE,"f3070712-bb4c-4e14-84f0-c401675ae4b3.3"),sQuery(id+"F0.wireOp",EDGE,"f3070712-bb4c-4e14-84f0-c401675ae4b3.4"),sQuery(id+"F0.wireOp",EDGE,"f3070712-bb4c-4e14-84f0-c401675ae4b3.5"),sQuery(id+"F0.wireOp",EDGE,"E43"),sQuery(id+"F0.wireOp",EDGE,"E46"),sQuery(id+"F0.wireOp",EDGE,"E48"),sQuery(id+"F0.wireOp",EDGE,"E49"),sQuery(id+"F0.wireOp",EDGE,"E65"),sQuery(id+"F0.wireOp",EDGE,"E71"),sQuery(id+"F0.wireOp",EDGE,"E72"),sQuery(id+"F0.wireOp",EDGE,"E73.MirrorC"),sQuery(id+"F0.wireOp",EDGE,"E74.MirrorC"),sQuery(id+"F0.wireOp",EDGE,"E76")])],"isStart":false});
            var sketch = newSketch(context, id + "F13", { "sketchPlane" : qUnion([Q0])});
            skArc(sketch, "E109.0", {"start": v(11.52, 8.93) * mm, "mid": v(0.51, 14.57) * mm, "end": v(-10.86, 9.72) * mm});
            skArc(sketch, "E109.1", {"start": v(-11.87, -8.46) * mm, "mid": v(-2.29, -14.4) * mm, "end": v(8.66, -11.72) * mm});
            skCircle(sketch, "E109.2", {"center": v(0, 0) * mm, "radius": 11.07 * mm});
            skLineSegment(sketch, "E110.0", {"start": v(-44.7, -8.46) * mm, "end": v(-11.87, -8.46) * mm});
            skLineSegment(sketch, "E110.1", {"start": v(-10.86, 9.72) * mm, "end": v(-28.69, 9.72) * mm});
            skArc(sketch, "E110.2", {"start": v(42.58, 16.03) * mm, "mid": v(-12.29, 43.8) * mm, "end": v(-44.7, -8.46) * mm});
            skLineSegment(sketch, "E111", {"start": v(0, 0) * mm, "end": v(0, 60.08) * mm, "construction": true});
            skLineSegment(sketch, "E112", {"start": v(0, 0) * mm, "end": v(0, -53.1) * mm, "construction": true});
            skLineSegment(sketch, "E113", {"start": v(0, 0) * mm, "end": v(16.07, 0) * mm, "construction": true});
            skLineSegment(sketch, "E114", {"start": v(0, 0) * mm, "end": v(-13.6, 0) * mm, "construction": true});
            skArc(sketch, "E115", {"start": v(-12.98, 6.63) * mm, "mid": v(-14.17, 3.4) * mm, "end": v(-14.57, 0) * mm});
            skArc(sketch, "E116", {"start": v(-11.87, -8.46) * mm, "mid": v(-2.21, -14.4) * mm, "end": v(8.78, -11.63) * mm, "construction": true});
            skArc(sketch, "E117", {"start": v(11.43, 9.04) * mm, "mid": v(0.45, 14.57) * mm, "end": v(-10.86, 9.72) * mm, "construction": true});
            skArc(sketch, "E118", {"start": v(12.98, -6.63) * mm, "mid": v(14.57, 0) * mm, "end": v(12.98, 6.63) * mm});
            skArc(sketch, "E119", {"start": v(-14.59, 6.46) * mm, "mid": v(-15.7, 3.31) * mm, "end": v(-16.07, 0) * mm});
            skArc(sketch, "E120.1.0.0", {"start": v(-20.15, 5.86) * mm, "mid": v(-21.06, 3) * mm, "end": v(-21.37, 0) * mm});
            skArc(sketch, "E120.1.0.1", {"start": v(-21.74, 5.69) * mm, "mid": v(-22.6, 2.9) * mm, "end": v(-22.87, 0) * mm});
            skArc(sketch, "E120.2.0.0", {"start": v(-27.26, 5.1) * mm, "mid": v(-27.94, 2.59) * mm, "end": v(-28.17, 0) * mm});
            skArc(sketch, "E120.2.0.1", {"start": v(-28.83, 4.92) * mm, "mid": v(-29.47, 2.5) * mm, "end": v(-29.67, 0) * mm});
            skArc(sketch, "E120.3.0.0", {"start": v(-34.31, 4.33) * mm, "mid": v(-34.8, 2.2) * mm, "end": v(-34.97, 0) * mm});
            skArc(sketch, "E120.3.0.1", {"start": v(-35.88, 4.17) * mm, "mid": v(-36.33, 2.1) * mm, "end": v(-36.47, 0) * mm});
            skArc(sketch, "E120.4.0.0", {"start": v(-41.33, 3.58) * mm, "mid": v(-41.66, 1.8) * mm, "end": v(-41.77, 0) * mm});
            skArc(sketch, "E120.4.0.1", {"start": v(-42.88, 3.41) * mm, "mid": v(-43.18, 1.72) * mm, "end": v(-43.27, 0) * mm});
            skLineSegment(sketch, "E121.trimOffspring", {"start": v(-44.45, 0) * mm, "end": v(-61.82, 0) * mm, "construction": true});
            skLineSegment(sketch, "E122", {"start": v(-42.88, 3.41) * mm, "end": v(-41.33, 3.58) * mm});
            skLineSegment(sketch, "E123.trimOffspring", {"start": v(-35.88, 4.17) * mm, "end": v(-34.31, 4.33) * mm});
            skLineSegment(sketch, "E124.trimOffspring", {"start": v(-28.83, 4.92) * mm, "end": v(-27.26, 5.1) * mm});
            skLineSegment(sketch, "E125.trimOffspring", {"start": v(-21.74, 5.69) * mm, "end": v(-20.15, 5.86) * mm});
            skLineSegment(sketch, "E126.trimOffspring", {"start": v(-14.59, 6.46) * mm, "end": v(-12.98, 6.63) * mm});
            skArc(sketch, "E127.MirrorCS", {"start": v(-42.88, -3.41) * mm, "mid": v(-43.18, -1.72) * mm, "end": v(-43.27, 0) * mm});
            skLineSegment(sketch, "E128.MirrorCS", {"start": v(-42.88, -3.41) * mm, "end": v(-41.33, -3.58) * mm});
            skArc(sketch, "E129.MirrorCS", {"start": v(-41.33, -3.58) * mm, "mid": v(-41.66, -1.8) * mm, "end": v(-41.77, 0) * mm});
            skArc(sketch, "E130.MirrorCS", {"start": v(-12.98, -6.63) * mm, "mid": v(-14.17, -3.4) * mm, "end": v(-14.57, 0) * mm});
            skLineSegment(sketch, "E131.MirrorCS", {"start": v(-14.59, -6.46) * mm, "end": v(-12.98, -6.63) * mm});
            skArc(sketch, "E132.MirrorCS", {"start": v(-14.59, -6.46) * mm, "mid": v(-15.7, -3.31) * mm, "end": v(-16.07, 0) * mm});
            skArc(sketch, "E133.MirrorCS", {"start": v(-20.15, -5.86) * mm, "mid": v(-21.06, -3) * mm, "end": v(-21.37, 0) * mm});
            skArc(sketch, "E134.MirrorCS", {"start": v(-21.74, -5.69) * mm, "mid": v(-22.6, -2.9) * mm, "end": v(-22.87, 0) * mm});
            skLineSegment(sketch, "E135.MirrorCS", {"start": v(-21.74, -5.69) * mm, "end": v(-20.15, -5.86) * mm});
            skArc(sketch, "E136.MirrorCS", {"start": v(-27.26, -5.1) * mm, "mid": v(-27.94, -2.59) * mm, "end": v(-28.17, 0) * mm});
            skArc(sketch, "E137.MirrorCS", {"start": v(-28.83, -4.92) * mm, "mid": v(-29.47, -2.5) * mm, "end": v(-29.67, 0) * mm});
            skLineSegment(sketch, "E138.MirrorCS", {"start": v(-28.83, -4.92) * mm, "end": v(-27.26, -5.1) * mm});
            skArc(sketch, "E139.MirrorCS", {"start": v(-34.31, -4.33) * mm, "mid": v(-34.8, -2.2) * mm, "end": v(-34.97, 0) * mm});
            skArc(sketch, "E140.MirrorCS", {"start": v(-35.88, -4.17) * mm, "mid": v(-36.33, -2.1) * mm, "end": v(-36.47, 0) * mm});
            skLineSegment(sketch, "E141.MirrorCS", {"start": v(-35.88, -4.17) * mm, "end": v(-34.31, -4.33) * mm});
            skArc(sketch, "E142.MirrorCS", {"start": v(35.88, 4.17) * mm, "mid": v(36.33, 2.1) * mm, "end": v(36.47, 0) * mm});
            skLineSegment(sketch, "E143.MirrorCS", {"start": v(21.74, -5.69) * mm, "end": v(20.15, -5.86) * mm});
            skLineSegment(sketch, "E144.MirrorCS", {"start": v(35.88, 4.17) * mm, "end": v(34.31, 4.33) * mm});
            skArc(sketch, "E145.MirrorCS", {"start": v(42.88, -3.41) * mm, "mid": v(43.18, -1.72) * mm, "end": v(43.27, 0) * mm});
            skLineSegment(sketch, "E146.MirrorCS", {"start": v(14.59, -6.46) * mm, "end": v(12.98, -6.63) * mm});
            skLineSegment(sketch, "E147.MirrorCS", {"start": v(14.59, 6.46) * mm, "end": v(12.98, 6.63) * mm});
            skLineSegment(sketch, "E148.MirrorCS", {"start": v(35.88, -4.17) * mm, "end": v(34.31, -4.33) * mm});
            skLineSegment(sketch, "E149.MirrorCS", {"start": v(42.88, -3.41) * mm, "end": v(41.33, -3.58) * mm});
            skArc(sketch, "E150.MirrorCS", {"start": v(41.33, -3.58) * mm, "mid": v(41.66, -1.8) * mm, "end": v(41.77, 0) * mm});
            skArc(sketch, "E151.MirrorCS", {"start": v(42.88, 3.41) * mm, "mid": v(43.18, 1.72) * mm, "end": v(43.27, 0) * mm});
            skArc(sketch, "E152.MirrorCS", {"start": v(34.31, 4.33) * mm, "mid": v(34.8, 2.2) * mm, "end": v(34.97, 0) * mm});
            skLineSegment(sketch, "E153.MirrorCS", {"start": v(42.88, 3.41) * mm, "end": v(41.33, 3.58) * mm});
            skLineSegment(sketch, "E154.MirrorCS", {"start": v(28.83, 4.92) * mm, "end": v(27.26, 5.1) * mm});
            skLineSegment(sketch, "E155.MirrorCS", {"start": v(28.83, -4.92) * mm, "end": v(27.26, -5.1) * mm});
            skLineSegment(sketch, "E156.MirrorCS", {"start": v(21.74, 5.69) * mm, "end": v(20.15, 5.86) * mm});
            skArc(sketch, "E157.MirrorCS", {"start": v(41.33, 3.58) * mm, "mid": v(41.66, 1.8) * mm, "end": v(41.77, 0) * mm});
            skArc(sketch, "E158.MirrorCS", {"start": v(27.26, 5.1) * mm, "mid": v(27.94, 2.59) * mm, "end": v(28.17, 0) * mm});
            skArc(sketch, "E159.MirrorCS", {"start": v(21.74, -5.69) * mm, "mid": v(22.6, -2.9) * mm, "end": v(22.87, 0) * mm});
            skArc(sketch, "E160.MirrorCS", {"start": v(12.98, -6.63) * mm, "mid": v(14.17, -3.4) * mm, "end": v(14.57, 0) * mm});
            skArc(sketch, "E161.MirrorCS", {"start": v(20.15, 5.86) * mm, "mid": v(21.06, 3) * mm, "end": v(21.37, 0) * mm});
            skArc(sketch, "E162.MirrorCS", {"start": v(35.88, -4.17) * mm, "mid": v(36.33, -2.1) * mm, "end": v(36.47, 0) * mm});
            skArc(sketch, "E163.MirrorCS", {"start": v(21.74, 5.69) * mm, "mid": v(22.6, 2.9) * mm, "end": v(22.87, 0) * mm});
            skArc(sketch, "E164.MirrorCS", {"start": v(14.59, 6.46) * mm, "mid": v(15.7, 3.31) * mm, "end": v(16.07, 0) * mm});
            skArc(sketch, "E165.MirrorCS", {"start": v(14.59, -6.46) * mm, "mid": v(15.7, -3.31) * mm, "end": v(16.07, 0) * mm});
            skArc(sketch, "E166.MirrorCS", {"start": v(28.83, 4.92) * mm, "mid": v(29.47, 2.5) * mm, "end": v(29.67, 0) * mm});
            skArc(sketch, "E167.MirrorCS", {"start": v(12.98, 6.63) * mm, "mid": v(14.17, 3.4) * mm, "end": v(14.57, 0) * mm});
            skArc(sketch, "E168.MirrorCS", {"start": v(28.83, -4.92) * mm, "mid": v(29.47, -2.5) * mm, "end": v(29.67, 0) * mm});
            skArc(sketch, "E169.MirrorCS", {"start": v(27.26, -5.1) * mm, "mid": v(27.94, -2.59) * mm, "end": v(28.17, 0) * mm});
            skArc(sketch, "E170.MirrorCS", {"start": v(20.15, -5.86) * mm, "mid": v(21.06, -3) * mm, "end": v(21.37, 0) * mm});
            skArc(sketch, "E171.MirrorCS", {"start": v(34.31, -4.33) * mm, "mid": v(34.8, -2.2) * mm, "end": v(34.97, 0) * mm});
            skArc(sketch, "E172.trimOffspring", {"start": v(11.52, 8.93) * mm, "mid": v(11.48, 8.98) * mm, "end": v(11.43, 9.04) * mm});
            skLineSegment(sketch, "E173.trimOffspring", {"start": v(20.4, 0) * mm, "end": v(22.87, 0) * mm, "construction": true});
            skLineSegment(sketch, "E174.trimOffspring", {"start": v(27.2, 0) * mm, "end": v(29.67, 0) * mm, "construction": true});
            skLineSegment(sketch, "E175.trimOffspring", {"start": v(34.97, 0) * mm, "end": v(36.47, 0) * mm, "construction": true});
            skLineSegment(sketch, "E176.trimOffspring", {"start": v(41.77, 0) * mm, "end": v(43.27, 0) * mm, "construction": true});
            skSolve(sketch);
        }
        {
            var Q0;
            Q0=makeQuery(id+"F13.imprint","IMPRINT",FACE,{"disambiguationData":[TD([[makeQuery(id+"F13.imprint","IMPRINT",EDGE,{"derivedFrom":sQuery(id+"F13.wireOp",EDGE,"E120.4.0.0")}),-1.0]])]});
            var Q1;
            Q1=makeQuery(id+"F13.imprint","IMPRINT",FACE,{"disambiguationData":[TD([[makeQuery(id+"F13.imprint","IMPRINT",EDGE,{"derivedFrom":sQuery(id+"F13.wireOp",EDGE,"E120.3.0.0")}),-1.0]])]});
            var Q2;
            Q2=makeQuery(id+"F13.imprint","IMPRINT",FACE,{"disambiguationData":[TD([[makeQuery(id+"F13.imprint","IMPRINT",EDGE,{"derivedFrom":sQuery(id+"F13.wireOp",EDGE,"E120.2.0.0")}),-1.0]])]});
            var Q3;
            Q3=makeQuery(id+"F13.imprint","IMPRINT",FACE,{"disambiguationData":[TD([[makeQuery(id+"F13.imprint","IMPRINT",EDGE,{"derivedFrom":sQuery(id+"F13.wireOp",EDGE,"E120.1.0.0")}),-1.0]])]});
            var Q4;
            Q4=makeQuery(id+"F13.imprint","IMPRINT",FACE,{"disambiguationData":[TD([[makeQuery(id+"F13.imprint","IMPRINT",EDGE,{"derivedFrom":sQuery(id+"F13.wireOp",EDGE,"E115")}),-1.0]])]});
            var Q5;
            Q5=makeQuery(id+"F13.imprint","IMPRINT",FACE,{"disambiguationData":[TD([[makeQuery(id+"F13.imprint","IMPRINT",EDGE,{"derivedFrom":sQuery(id+"F13.wireOp",EDGE,"E146.MirrorCS")}),-1.0]])]});
            var Q6;
            Q6=makeQuery(id+"F13.imprint","IMPRINT",FACE,{"disambiguationData":[TD([[makeQuery(id+"F13.imprint","IMPRINT",EDGE,{"derivedFrom":sQuery(id+"F13.wireOp",EDGE,"E143.MirrorCS")}),-1.0]])]});
            var Q7;
            Q7=makeQuery(id+"F13.imprint","IMPRINT",FACE,{"disambiguationData":[TD([[makeQuery(id+"F13.imprint","IMPRINT",EDGE,{"derivedFrom":sQuery(id+"F13.wireOp",EDGE,"E154.MirrorCS")}),1.0]])]});
            var Q8;
            Q8=makeQuery(id+"F13.imprint","IMPRINT",FACE,{"disambiguationData":[TD([[makeQuery(id+"F13.imprint","IMPRINT",EDGE,{"derivedFrom":sQuery(id+"F13.wireOp",EDGE,"E142.MirrorCS")}),-1.0]])]});
            var Q9;
            Q9=makeQuery(id+"F13.imprint","IMPRINT",FACE,{"disambiguationData":[TD([[makeQuery(id+"F13.imprint","IMPRINT",EDGE,{"derivedFrom":sQuery(id+"F13.wireOp",EDGE,"E145.MirrorCS")}),1.0]])]});
            extrude(context, id + "F14", {"entities" : qUnion([Q0, Q1, Q2, Q3, Q4, Q5, Q6, Q7, Q8, Q9]), "operationType" : NewBodyOperationType.REMOVE, "endBound" : BoundingType.THROUGH_ALL, "oppositeDirection" : true, "depth" : 25 * mm, "offsetDistance" : 25 * mm});
        }
    });
